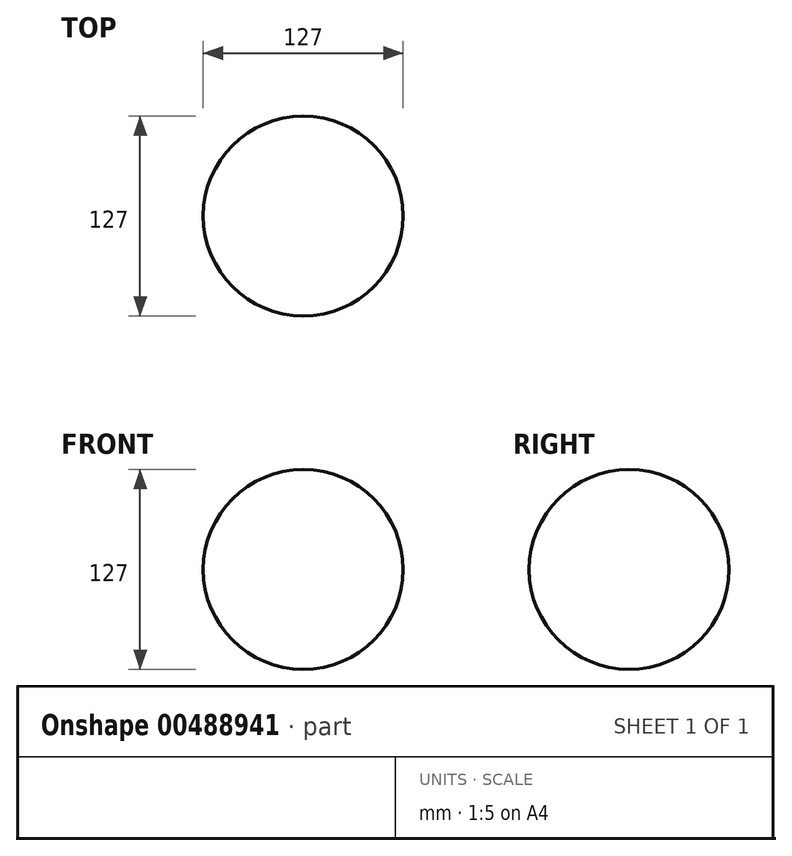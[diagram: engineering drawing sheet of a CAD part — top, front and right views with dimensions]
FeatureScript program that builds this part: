
annotation { "Feature Type Name" : "Feature", "Feature Type Description" : "" }
export const myFeature = defineFeature(function(context is Context, id is Id, definition is map)
    precondition{}
    {
        {
            var Q0;
            Q0=qCreatedBy(makeId("Front.planeOp"),FACE);
            var sketch = newSketch(context, id + "F0", { "sketchPlane" : qUnion([Q0])});
            skArc(sketch, "E0", {"start": v(0, -63.5) * mm, "mid": v(63.5, 0) * mm, "end": v(0, 63.5) * mm});
            skLineSegment(sketch, "E1", {"start": v(0, 63.5) * mm, "end": v(0, -63.5) * mm});
            skSolve(sketch);
        }
        {
            var Q0;
            Q0 = qSketchRegion(id + "F0", true);
            var Q1;
            Q1=sQuery(id+"F0.wireOp",EDGE,"E1");
            revolve(context, id + "F1", {"entities" : qUnion([Q0]), "axis" : qUnion([Q1]), "revolveType" : RevolveType.FULL});
        }
    });
